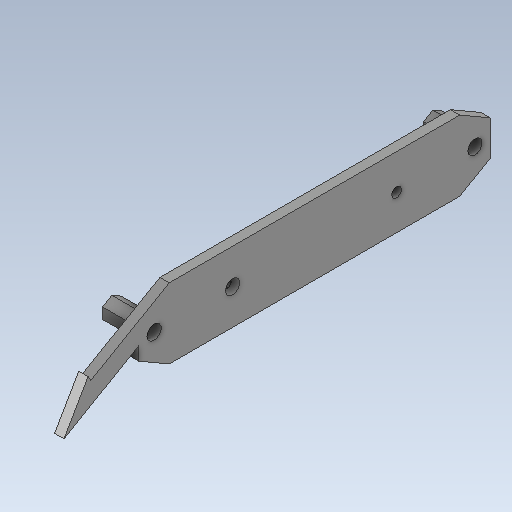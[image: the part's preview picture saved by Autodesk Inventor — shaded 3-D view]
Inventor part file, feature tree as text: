
AUTODESK INVENTOR PART (.ipt)
format: ipt  version: 2020 (Build 240168000, 168)  size: 162,816 bytes
history: native  units: in
note: dims shown in document units (in); Inventor stores cm internally (conversion verified against a paired STEP export)
features: other x3, extrude x1, sketch x1
ambient origin geometry x8: Origin, YZ Plane, XZ Plane, XY Plane, X Axis, Y Axis, Z Axis, Center Point
bodies: Solid1 (feature_tree)
feature tree (5):
  other  "HexWheelGuard.ipt"
  extrude  "Extrusion1"  Depth=0.315in
  other  "Solid1::HexWheelGuard.ipt"
  other  "TaggingFeature2"
  sketch  "Sketch1"  dims[d1=0.3937in d2=0.315in d3=60.0deg d4=1.3858in d5=0.0787in d6=0.3937in d7=0.0in]
